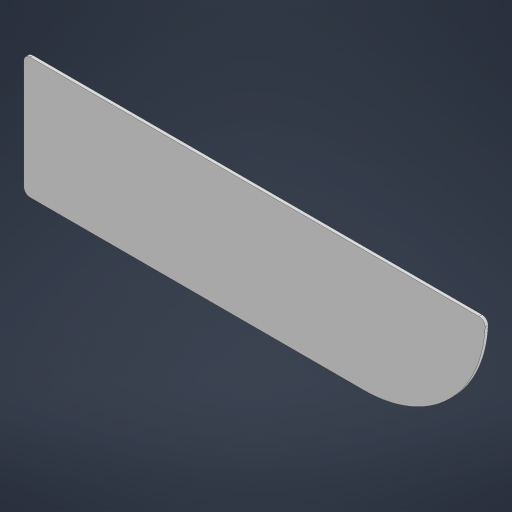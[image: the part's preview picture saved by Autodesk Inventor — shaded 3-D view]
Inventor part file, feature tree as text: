
AUTODESK INVENTOR PART (.ipt)
format: ipt  version: 2023 (Build 270158000, 158)  size: 164,352 bytes
history: native  units: in
note: dims shown in document units (in); Inventor stores cm internally (conversion verified against a paired STEP export)
features: fillet x3, extrude x1, sketch x1
ambient origin geometry x8: Origin, YZ Plane, XZ Plane, XY Plane, X Axis, Y Axis, Z Axis, Center Point
bodies: Solid1 (feature_tree)
feature tree (5):
  extrude  "Extrusion1"  Depth=7.0in
  fillet  "Fillet1"  Radius=7.0in
  fillet  "Fillet2"  Radius=0.0625in
  fillet  "Fillet3"  Radius=0.125in
  sketch  "Sketch1"  dims[d0=5.0in d1=7.0in d2=7.0in d3=0.0625in d4=0.0in d5=0.125in d6=0.125in d7=0.125in]
